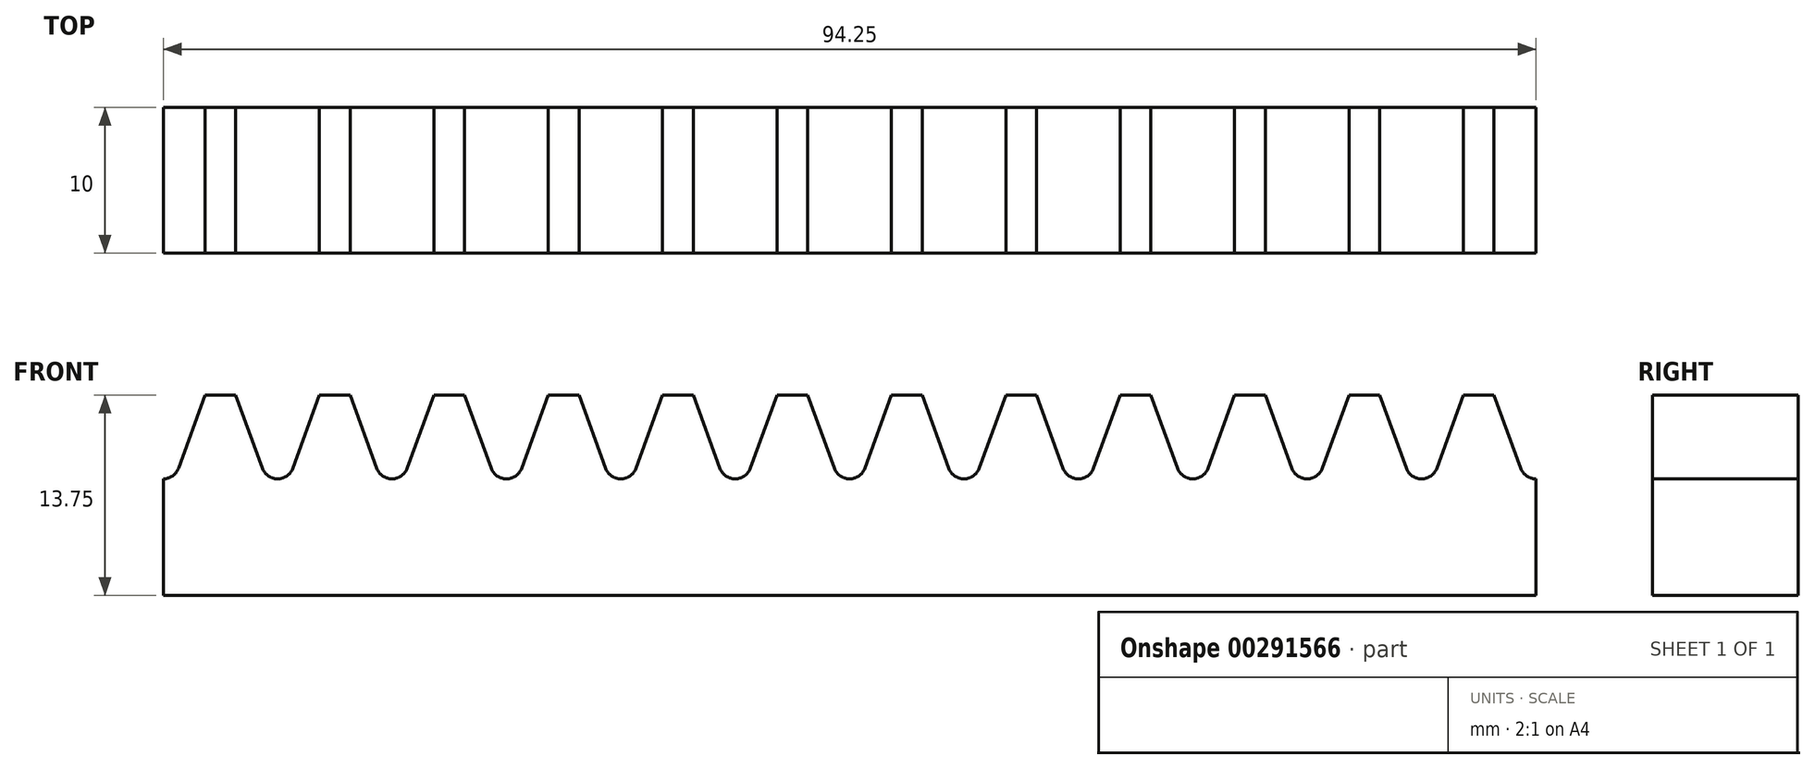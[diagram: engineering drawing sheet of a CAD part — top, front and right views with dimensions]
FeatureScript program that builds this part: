
annotation { "Feature Type Name" : "Feature", "Feature Type Description" : "" }
export const myFeature = defineFeature(function(context is Context, id is Id, definition is map)
    precondition{}
    {
        {
            var Q0;
            Q0=qCreatedBy(makeId("Front.planeOp"),FACE);
            var sketch = newSketch(context, id + "F0", { "sketchPlane" : qUnion([Q0])});
            skLineSegment(sketch, "E0", {"start": v(0, 0) * mm, "end": v(0, -9.11) * mm, "construction": true});
            skLineSegment(sketch, "E1", {"start": v(1.05, -8.73) * mm, "end": v(2.87, -13.75) * mm, "construction": true});
            skLineSegment(sketch, "E2", {"start": v(2.87, -13.75) * mm, "end": v(4.98, -13.75) * mm, "construction": true});
            skLineSegment(sketch, "E3", {"start": v(4.98, -13.75) * mm, "end": v(6.8, -8.73) * mm, "construction": true});
            skLineSegment(sketch, "E4", {"start": v(8.9, -8.73) * mm, "end": v(10.73, -13.75) * mm, "construction": true});
            skLineSegment(sketch, "E5", {"start": v(10.73, -13.75) * mm, "end": v(12.83, -13.75) * mm, "construction": true});
            skLineSegment(sketch, "E6", {"start": v(12.83, -13.75) * mm, "end": v(14.66, -8.73) * mm, "construction": true});
            skLineSegment(sketch, "E7", {"start": v(16.76, -8.73) * mm, "end": v(18.58, -13.75) * mm, "construction": true});
            skLineSegment(sketch, "E8", {"start": v(18.58, -13.75) * mm, "end": v(20.69, -13.75) * mm, "construction": true});
            skLineSegment(sketch, "E9", {"start": v(20.69, -13.75) * mm, "end": v(22.51, -8.73) * mm, "construction": true});
            skLineSegment(sketch, "E10", {"start": v(24.6, -8.73) * mm, "end": v(26.44, -13.75) * mm, "construction": true});
            skLineSegment(sketch, "E11", {"start": v(26.44, -13.75) * mm, "end": v(28.54, -13.75) * mm, "construction": true});
            skLineSegment(sketch, "E12", {"start": v(28.54, -13.75) * mm, "end": v(30.37, -8.73) * mm, "construction": true});
            skLineSegment(sketch, "E13", {"start": v(0, -11.25) * mm, "end": v(31.44, -11.25) * mm, "construction": true});
            skArc(sketch, "E14", {"start": v(24.6, -8.73) * mm, "mid": v(23.56, -8) * mm, "end": v(22.51, -8.73) * mm, "construction": true});
            skArc(sketch, "E15", {"start": v(16.76, -8.73) * mm, "mid": v(15.7, -8) * mm, "end": v(14.66, -8.73) * mm, "construction": true});
            skArc(sketch, "E16", {"start": v(8.9, -8.73) * mm, "mid": v(7.85, -8) * mm, "end": v(6.8, -8.73) * mm, "construction": true});
            skLineSegment(sketch, "E17", {"start": v(31.42, -8) * mm, "end": v(31.42, 0) * mm, "construction": true});
            skArc(sketch, "E18", {"start": v(31.42, -8) * mm, "mid": v(30.78, -8.2) * mm, "end": v(30.37, -8.73) * mm, "construction": true});
            skPoint(sketch, "E19.MirrorCS.start.orphan", {"position": v(31.42, -8) * mm});
            skLineSegment(sketch, "E20", {"start": v(0, 0) * mm, "end": v(31.42, 0) * mm});
            skLineSegment(sketch, "E21", {"start": v(31.42, -9.11) * mm, "end": v(-1.97, -9.11) * mm, "construction": true});
            skLineSegment(sketch, "E22", {"start": v(13.74, -11.25) * mm, "end": v(13.74, -15.1) * mm, "construction": true});
            skLineSegment(sketch, "E23", {"start": v(17.67, -11.25) * mm, "end": v(17.67, -15.1) * mm, "construction": true});
            skLineSegment(sketch, "E24", {"start": v(21.6, -11.25) * mm, "end": v(21.6, -15.32) * mm, "construction": true});
            skArc(sketch, "E25", {"start": v(1.05, -8.73) * mm, "mid": v(0.64, -8.2) * mm, "end": v(0, -8) * mm, "construction": true});
            skLineSegment(sketch, "E26", {"start": v(31.42, -9.11) * mm, "end": v(31.42, -8) * mm, "construction": true});
            skArc(sketch, "E27.MirrorCS", {"start": v(31.42, -8) * mm, "mid": v(32.06, -8.2) * mm, "end": v(32.46, -8.73) * mm, "construction": true});
            skArc(sketch, "E28.MirrorCS", {"start": v(61.78, -8.73) * mm, "mid": v(62.2, -8.2) * mm, "end": v(62.83, -8) * mm, "construction": true});
            skLineSegment(sketch, "E29.MirrorCS", {"start": v(59.96, -13.75) * mm, "end": v(57.85, -13.75) * mm, "construction": true});
            skArc(sketch, "E30.MirrorCS", {"start": v(53.93, -8.73) * mm, "mid": v(54.98, -8) * mm, "end": v(56.03, -8.73) * mm, "construction": true});
            skLineSegment(sketch, "E31.MirrorCS", {"start": v(62.83, -11.25) * mm, "end": v(31.4, -11.25) * mm, "construction": true});
            skLineSegment(sketch, "E32.MirrorCS", {"start": v(62.83, 0) * mm, "end": v(31.42, 0) * mm});
            skLineSegment(sketch, "E33.MirrorCS", {"start": v(61.78, -8.73) * mm, "end": v(59.96, -13.75) * mm, "construction": true});
            skLineSegment(sketch, "E34.MirrorCS", {"start": v(50, -13.75) * mm, "end": v(48.17, -8.73) * mm, "construction": true});
            skLineSegment(sketch, "E35.MirrorCS", {"start": v(46.08, -8.73) * mm, "end": v(44.25, -13.75) * mm, "construction": true});
            skLineSegment(sketch, "E36.MirrorCS", {"start": v(57.85, -13.75) * mm, "end": v(56.03, -8.73) * mm, "construction": true});
            skLineSegment(sketch, "E37.MirrorCS", {"start": v(45.16, -11.25) * mm, "end": v(45.16, -15.1) * mm, "construction": true});
            skLineSegment(sketch, "E38.MirrorCS", {"start": v(62.83, 0) * mm, "end": v(62.83, -9.11) * mm, "construction": true});
            skLineSegment(sketch, "E39.MirrorCS", {"start": v(36.4, -13.75) * mm, "end": v(34.29, -13.75) * mm, "construction": true});
            skLineSegment(sketch, "E40.MirrorCS", {"start": v(41.23, -11.25) * mm, "end": v(41.23, -15.32) * mm, "construction": true});
            skLineSegment(sketch, "E41.MirrorCS", {"start": v(53.93, -8.73) * mm, "end": v(52.1, -13.75) * mm, "construction": true});
            skLineSegment(sketch, "E42.MirrorCS", {"start": v(42.14, -13.75) * mm, "end": v(40.32, -8.73) * mm, "construction": true});
            skLineSegment(sketch, "E43.MirrorCS", {"start": v(49.09, -11.25) * mm, "end": v(49.09, -15.1) * mm, "construction": true});
            skLineSegment(sketch, "E44.MirrorCS", {"start": v(34.29, -13.75) * mm, "end": v(32.46, -8.73) * mm, "construction": true});
            skLineSegment(sketch, "E45.MirrorCS", {"start": v(52.1, -13.75) * mm, "end": v(50, -13.75) * mm, "construction": true});
            skLineSegment(sketch, "E46.MirrorCS", {"start": v(44.25, -13.75) * mm, "end": v(42.14, -13.75) * mm, "construction": true});
            skLineSegment(sketch, "E47.MirrorCS", {"start": v(38.22, -8.73) * mm, "end": v(36.4, -13.75) * mm, "construction": true});
            skArc(sketch, "E48.MirrorCS", {"start": v(38.22, -8.73) * mm, "mid": v(39.27, -8) * mm, "end": v(40.32, -8.73) * mm, "construction": true});
            skArc(sketch, "E49.MirrorCS", {"start": v(46.08, -8.73) * mm, "mid": v(47.12, -8) * mm, "end": v(48.17, -8.73) * mm, "construction": true});
            skLineSegment(sketch, "E50.MirrorCS", {"start": v(31.42, -9.11) * mm, "end": v(64.8, -9.11) * mm, "construction": true});
            skLineSegment(sketch, "E51.MirrorCS", {"start": v(31.42, 9.11) * mm, "end": v(31.42, 8) * mm});
            skArc(sketch, "E52.MirrorCS", {"start": v(31.42, 8) * mm, "mid": v(30.78, 8.2) * mm, "end": v(30.37, 8.73) * mm});
            skArc(sketch, "E53.MirrorCS", {"start": v(31.42, 8) * mm, "mid": v(32.06, 8.2) * mm, "end": v(32.46, 8.73) * mm});
            skPoint(sketch, "E54.MirrorP", {"position": v(31.42, 8) * mm});
            skArc(sketch, "E55.MirrorCS", {"start": v(16.76, 8.73) * mm, "mid": v(15.7, 8) * mm, "end": v(14.66, 8.73) * mm});
            skLineSegment(sketch, "E56.MirrorCS", {"start": v(44.25, 13.75) * mm, "end": v(42.14, 13.75) * mm});
            skArc(sketch, "E57.MirrorCS", {"start": v(24.6, 8.73) * mm, "mid": v(23.56, 8) * mm, "end": v(22.51, 8.73) * mm});
            skArc(sketch, "E58.MirrorCS", {"start": v(38.22, 8.73) * mm, "mid": v(39.27, 8) * mm, "end": v(40.32, 8.73) * mm});
            skLineSegment(sketch, "E59.MirrorCS", {"start": v(52.1, 13.75) * mm, "end": v(50, 13.75) * mm});
            skLineSegment(sketch, "E60.MirrorCS", {"start": v(34.29, 13.75) * mm, "end": v(32.46, 8.73) * mm});
            skLineSegment(sketch, "E61.MirrorCS", {"start": v(12.83, 13.75) * mm, "end": v(14.66, 8.73) * mm});
            skArc(sketch, "E62.MirrorCS", {"start": v(8.9, 8.73) * mm, "mid": v(7.85, 8) * mm, "end": v(6.8, 8.73) * mm});
            skLineSegment(sketch, "E63.MirrorCS", {"start": v(46.08, 8.73) * mm, "end": v(44.25, 13.75) * mm});
            skLineSegment(sketch, "E64.MirrorCS", {"start": v(42.14, 13.75) * mm, "end": v(40.32, 8.73) * mm});
            skArc(sketch, "E65.MirrorCS", {"start": v(61.78, 8.73) * mm, "mid": v(62.2, 8.2) * mm, "end": v(62.83, 8) * mm});
            skLineSegment(sketch, "E66.MirrorCS", {"start": v(41.23, 11.25) * mm, "end": v(41.23, 15.32) * mm, "construction": true});
            skLineSegment(sketch, "E67.MirrorCS", {"start": v(50, 13.75) * mm, "end": v(48.17, 8.73) * mm});
            skArc(sketch, "E68.MirrorCS", {"start": v(46.08, 8.73) * mm, "mid": v(47.12, 8) * mm, "end": v(48.17, 8.73) * mm});
            skLineSegment(sketch, "E69.MirrorCS", {"start": v(59.96, 13.75) * mm, "end": v(57.85, 13.75) * mm});
            skLineSegment(sketch, "E70.MirrorCS", {"start": v(16.76, 8.73) * mm, "end": v(18.58, 13.75) * mm});
            skLineSegment(sketch, "E71.MirrorCS", {"start": v(28.54, 13.75) * mm, "end": v(30.37, 8.73) * mm});
            skLineSegment(sketch, "E72.MirrorCS", {"start": v(36.4, 13.75) * mm, "end": v(34.29, 13.75) * mm});
            skLineSegment(sketch, "E73.MirrorCS", {"start": v(26.44, 13.75) * mm, "end": v(28.54, 13.75) * mm});
            skLineSegment(sketch, "E74.MirrorCS", {"start": v(61.78, 8.73) * mm, "end": v(59.96, 13.75) * mm});
            skArc(sketch, "E75.MirrorCS", {"start": v(1.05, 8.73) * mm, "mid": v(0.64, 8.2) * mm, "end": v(0, 8) * mm});
            skLineSegment(sketch, "E76.MirrorCS", {"start": v(17.67, 11.25) * mm, "end": v(17.67, 15.1) * mm, "construction": true});
            skLineSegment(sketch, "E77.MirrorCS", {"start": v(1.05, 8.73) * mm, "end": v(2.87, 13.75) * mm});
            skLineSegment(sketch, "E78.MirrorCS", {"start": v(4.98, 13.75) * mm, "end": v(6.8, 8.73) * mm});
            skLineSegment(sketch, "E79.MirrorCS", {"start": v(18.58, 13.75) * mm, "end": v(20.69, 13.75) * mm});
            skLineSegment(sketch, "E80.MirrorCS", {"start": v(45.16, 11.25) * mm, "end": v(45.16, 15.1) * mm, "construction": true});
            skLineSegment(sketch, "E81.MirrorCS", {"start": v(13.74, 11.25) * mm, "end": v(13.74, 15.1) * mm, "construction": true});
            skLineSegment(sketch, "E82.MirrorCS", {"start": v(21.6, 11.25) * mm, "end": v(21.6, 15.32) * mm, "construction": true});
            skLineSegment(sketch, "E83.MirrorCS", {"start": v(49.09, 11.25) * mm, "end": v(49.09, 15.1) * mm, "construction": true});
            skLineSegment(sketch, "E84.MirrorCS", {"start": v(62.83, 11.25) * mm, "end": v(31.4, 11.25) * mm, "construction": true});
            skLineSegment(sketch, "E85.MirrorCS", {"start": v(38.22, 8.73) * mm, "end": v(36.4, 13.75) * mm});
            skLineSegment(sketch, "E86.MirrorCS", {"start": v(24.6, 8.73) * mm, "end": v(26.44, 13.75) * mm});
            skLineSegment(sketch, "E87.MirrorCS", {"start": v(31.42, 9.11) * mm, "end": v(-1.97, 9.11) * mm, "construction": true});
            skLineSegment(sketch, "E88.MirrorCS", {"start": v(0, 11.25) * mm, "end": v(31.44, 11.25) * mm, "construction": true});
            skLineSegment(sketch, "E89.MirrorCS", {"start": v(2.87, 13.75) * mm, "end": v(4.98, 13.75) * mm});
            skLineSegment(sketch, "E90.MirrorCS", {"start": v(57.85, 13.75) * mm, "end": v(56.03, 8.73) * mm});
            skLineSegment(sketch, "E91.MirrorCS", {"start": v(8.9, 8.73) * mm, "end": v(10.73, 13.75) * mm});
            skLineSegment(sketch, "E92.MirrorCS", {"start": v(10.73, 13.75) * mm, "end": v(12.83, 13.75) * mm});
            skArc(sketch, "E93.MirrorCS", {"start": v(53.93, 8.73) * mm, "mid": v(54.98, 8) * mm, "end": v(56.03, 8.73) * mm});
            skLineSegment(sketch, "E94.MirrorCS", {"start": v(53.93, 8.73) * mm, "end": v(52.1, 13.75) * mm});
            skLineSegment(sketch, "E95.MirrorCS", {"start": v(20.69, 13.75) * mm, "end": v(22.51, 8.73) * mm});
            skLineSegment(sketch, "E96.MirrorCS", {"start": v(31.42, 9.11) * mm, "end": v(64.8, 9.11) * mm, "construction": true});
            skLineSegment(sketch, "E97.MirrorCS", {"start": v(0, 0) * mm, "end": v(0, 9.11) * mm});
            skLineSegment(sketch, "E98.MirrorCS", {"start": v(62.83, 0) * mm, "end": v(62.83, 9.11) * mm});
            skLineSegment(sketch, "E99.MirrorCS", {"start": v(31.42, 8) * mm, "end": v(31.42, 0) * mm});
            skLineSegment(sketch, "E100.MirrorCS", {"start": v(94.25, 9.11) * mm, "end": v(94.25, 8) * mm});
            skArc(sketch, "E101.MirrorCS", {"start": v(94.25, 8) * mm, "mid": v(93.6, 8.2) * mm, "end": v(93.2, 8.73) * mm});
            skPoint(sketch, "E102.MirrorP", {"position": v(94.25, 8) * mm});
            skArc(sketch, "E103.MirrorCS", {"start": v(63.88, 8.73) * mm, "mid": v(63.47, 8.2) * mm, "end": v(62.83, 8) * mm});
            skLineSegment(sketch, "E104.MirrorCS", {"start": v(89.27, 13.75) * mm, "end": v(91.37, 13.75) * mm});
            skLineSegment(sketch, "E105.MirrorCS", {"start": v(81.41, 13.75) * mm, "end": v(83.52, 13.75) * mm});
            skLineSegment(sketch, "E106.MirrorCS", {"start": v(94.25, 9.11) * mm, "end": v(60.86, 9.11) * mm, "construction": true});
            skLineSegment(sketch, "E107.MirrorCS", {"start": v(83.52, 13.75) * mm, "end": v(85.35, 8.73) * mm});
            skLineSegment(sketch, "E108.MirrorCS", {"start": v(80.5, 11.25) * mm, "end": v(80.5, 15.1) * mm, "construction": true});
            skLineSegment(sketch, "E109.MirrorCS", {"start": v(79.59, 8.73) * mm, "end": v(81.41, 13.75) * mm});
            skLineSegment(sketch, "E110.MirrorCS", {"start": v(71.73, 8.73) * mm, "end": v(73.56, 13.75) * mm});
            skLineSegment(sketch, "E111.MirrorCS", {"start": v(94.25, 8) * mm, "end": v(94.25, 0) * mm});
            skLineSegment(sketch, "E112.MirrorCS", {"start": v(65.7, 13.75) * mm, "end": v(67.81, 13.75) * mm});
            skLineSegment(sketch, "E113.MirrorCS", {"start": v(87.44, 8.73) * mm, "end": v(89.27, 13.75) * mm});
            skArc(sketch, "E114.MirrorCS", {"start": v(71.73, 8.73) * mm, "mid": v(70.69, 8) * mm, "end": v(69.64, 8.73) * mm});
            skArc(sketch, "E115.MirrorCS", {"start": v(79.59, 8.73) * mm, "mid": v(78.54, 8) * mm, "end": v(77.5, 8.73) * mm});
            skLineSegment(sketch, "E116.MirrorCS", {"start": v(62.83, 11.25) * mm, "end": v(94.27, 11.25) * mm, "construction": true});
            skLineSegment(sketch, "E117.MirrorCS", {"start": v(73.56, 13.75) * mm, "end": v(75.67, 13.75) * mm});
            skLineSegment(sketch, "E118.MirrorCS", {"start": v(91.37, 13.75) * mm, "end": v(93.2, 8.73) * mm});
            skLineSegment(sketch, "E119.MirrorCS", {"start": v(75.67, 13.75) * mm, "end": v(77.5, 8.73) * mm});
            skLineSegment(sketch, "E120.MirrorCS", {"start": v(76.58, 11.25) * mm, "end": v(76.58, 15.1) * mm, "construction": true});
            skLineSegment(sketch, "E121.MirrorCS", {"start": v(63.88, 8.73) * mm, "end": v(65.7, 13.75) * mm});
            skLineSegment(sketch, "E122.MirrorCS", {"start": v(67.81, 13.75) * mm, "end": v(69.64, 8.73) * mm});
            skArc(sketch, "E123.MirrorCS", {"start": v(87.44, 8.73) * mm, "mid": v(86.4, 8) * mm, "end": v(85.35, 8.73) * mm});
            skLineSegment(sketch, "E124.MirrorCS", {"start": v(84.43, 11.25) * mm, "end": v(84.43, 15.32) * mm, "construction": true});
            skLineSegment(sketch, "E125.MirrorCS", {"start": v(62.83, 0) * mm, "end": v(94.25, 0) * mm});
            skSolve(sketch);
        }
        {
            var Q0;
            Q0 = qSketchRegion(id + "F0", true);
            extrude(context, id + "F1", {"entities" : qUnion([Q0]), "endBound" : BoundingType.SYMMETRIC, "depth" : 10 * mm});
        }
    });
